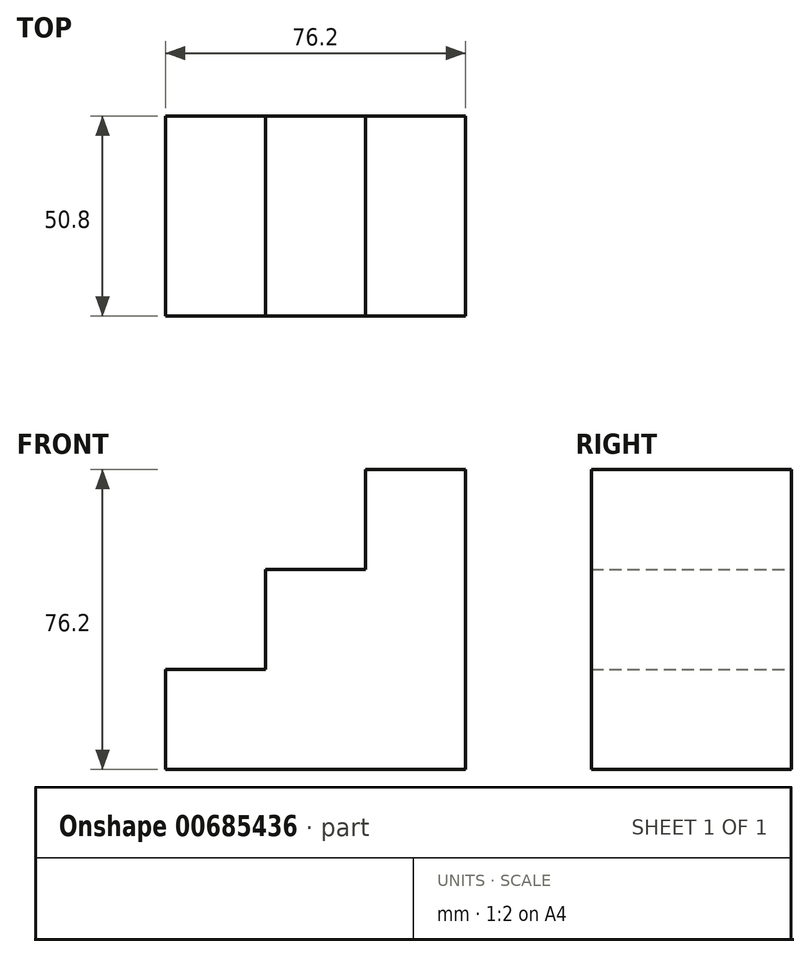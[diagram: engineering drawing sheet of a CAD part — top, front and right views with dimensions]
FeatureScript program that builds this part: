
annotation { "Feature Type Name" : "Feature", "Feature Type Description" : "" }
export const myFeature = defineFeature(function(context is Context, id is Id, definition is map)
    precondition{}
    {
        {
            var Q0;
            Q0=qCreatedBy(makeId("Front.planeOp"),FACE);
            var sketch = newSketch(context, id + "F0", { "sketchPlane" : qUnion([Q0])});
            skLineSegment(sketch, "E0", {"start": v(0, 64.1) * mm, "end": v(0, -12.1) * mm});
            skLineSegment(sketch, "E1", {"start": v(0, -12.1) * mm, "end": v(-76.2, -12.1) * mm});
            skLineSegment(sketch, "E2", {"start": v(-76.2, -12.1) * mm, "end": v(-76.2, 13.3) * mm});
            skLineSegment(sketch, "E3", {"start": v(-76.2, 13.3) * mm, "end": v(-50.8, 13.3) * mm});
            skLineSegment(sketch, "E4", {"start": v(-50.8, 13.3) * mm, "end": v(-50.8, 38.7) * mm});
            skLineSegment(sketch, "E5", {"start": v(-50.8, 38.7) * mm, "end": v(-25.4, 38.7) * mm});
            skLineSegment(sketch, "E6", {"start": v(-25.4, 38.7) * mm, "end": v(-25.4, 64.1) * mm});
            skLineSegment(sketch, "E7", {"start": v(-25.4, 64.1) * mm, "end": v(0, 64.1) * mm});
            skSolve(sketch);
        }
        {
            var Q0;
            Q0 = qSketchRegion(id + "F0", true);
            extrude(context, id + "F1", {"entities" : qUnion([Q0]), "depth" : 50.8 * mm, "offsetDistance" : 25.4 * mm});
        }
    });
